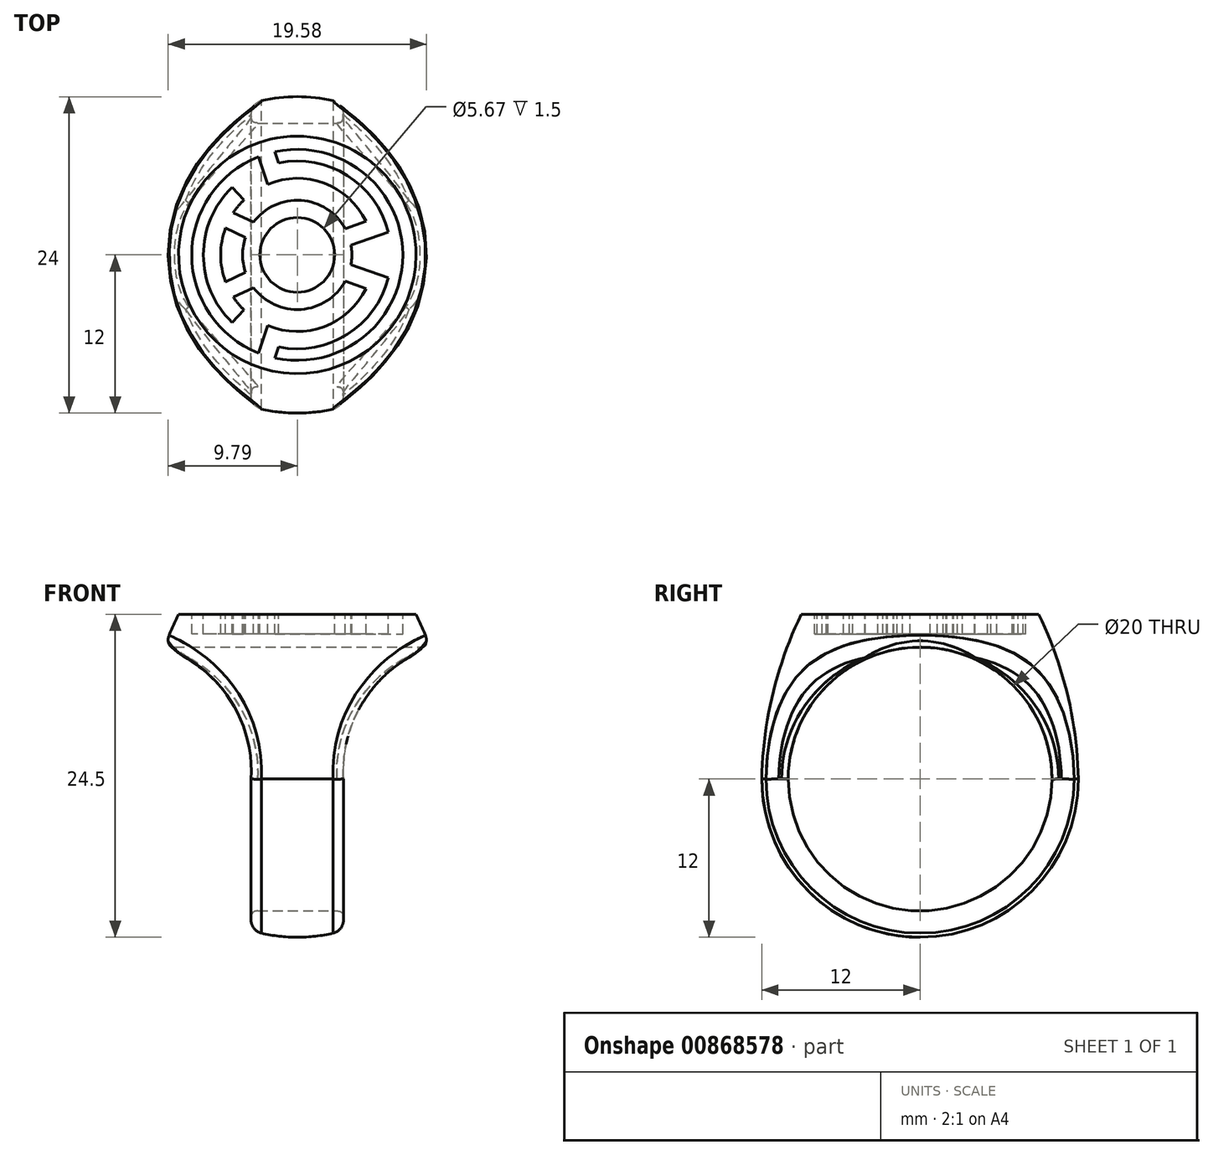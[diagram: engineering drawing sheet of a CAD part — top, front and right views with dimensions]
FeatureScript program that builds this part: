
annotation { "Feature Type Name" : "Feature", "Feature Type Description" : "" }
export const myFeature = defineFeature(function(context is Context, id is Id, definition is map)
    precondition{}
    {
        {
            var Q0;
            Q0=qCreatedBy(makeId("Right.planeOp"),FACE);
            var sketch = newSketch(context, id + "F0", { "sketchPlane" : qUnion([Q0])});
            skLineSegment(sketch, "E0", {"start": v(0, 0) * mm, "end": v(0, -24.5) * mm});
            skLineSegment(sketch, "E1", {"start": v(0, 0) * mm, "end": v(-9, 0) * mm});
            skArc(sketch, "E2", {"start": v(-12, -12.5) * mm, "mid": v(-8.49, -20.99) * mm, "end": v(0, -24.5) * mm});
            skLineSegment(sketch, "E3", {"start": v(0, -12.5) * mm, "end": v(-12, -12.5) * mm, "construction": true});
            skArc(sketch, "E4", {"start": v(-9, 0) * mm, "mid": v(-11.18, -6.09) * mm, "end": v(-12, -12.5) * mm});
            skSolve(sketch);
        }
        {
            var Q0;
            Q0=makeQuery(id+"F0.imprint","IMPRINT",FACE,{"disambiguationData":[TD([[makeQuery(id+"F0.imprint","IMPRINT",EDGE,{"derivedFrom":sQuery(id+"F0.wireOp",EDGE,"E0")}),-1.0]])]});
            var Q1;
            Q1=sQuery(id+"F0.wireOp",EDGE,"E0");
            revolve(context, id + "F1", {"entities" : qUnion([Q0]), "axis" : qUnion([Q1]), "revolveType" : RevolveType.FULL});
        }
        {
            var Q0;
            Q0=qCreatedBy(makeId("Right.planeOp"),FACE);
            var sketch = newSketch(context, id + "F2", { "sketchPlane" : qUnion([Q0])});
            skCircle(sketch, "E5", {"center": v(0, -12.5) * mm, "radius": 10 * mm});
            skSolve(sketch);
        }
        {
            var Q0;
            Q0=qSketchRegion(id+"F2",true);
            extrude(context, id + "F3", {"entities" : qUnion([Q0]), "operationType" : NewBodyOperationType.REMOVE, "endBound" : BoundingType.SYMMETRIC, "oppositeDirection" : true, "depth" : 25 * mm, "offsetDistance" : 25 * mm});
        }
        {
            var Q0;
            Q0=qCreatedBy(makeId("Front.planeOp"),FACE);
            var sketch = newSketch(context, id + "F4", { "sketchPlane" : qUnion([Q0])});
            skLineSegment(sketch, "E6", {"start": v(3.5, -26.5) * mm, "end": v(3.5, -12.5) * mm});
            skArc(sketch, "E7", {"start": v(10.15, -2.5) * mm, "mid": v(5.16, -6.39) * mm, "end": v(3.5, -12.5) * mm});
            skLineSegment(sketch, "E8", {"start": v(10.15, -2.5) * mm, "end": v(11.65, -2.5) * mm});
            skLineSegment(sketch, "E9", {"start": v(11.65, -2.5) * mm, "end": v(11.65, -26.5) * mm});
            skLineSegment(sketch, "E10", {"start": v(11.65, -26.5) * mm, "end": v(3.5, -26.5) * mm});
            skPoint(sketch, "E11.start.orphan", {"position": v(0, -24.5) * mm});
            skLineSegment(sketch, "E12", {"start": v(0, 0) * mm, "end": v(0, -24.5) * mm, "construction": true});
            skLineSegment(sketch, "E13.MirrorCS", {"start": v(-3.5, -26.5) * mm, "end": v(-3.5, -12.5) * mm});
            skArc(sketch, "E14.MirrorCS", {"start": v(-10.15, -2.5) * mm, "mid": v(-5.16, -6.39) * mm, "end": v(-3.5, -12.5) * mm});
            skLineSegment(sketch, "E15.MirrorCS", {"start": v(-11.65, -2.5) * mm, "end": v(-11.65, -26.5) * mm});
            skLineSegment(sketch, "E16.MirrorCS", {"start": v(-11.65, -26.5) * mm, "end": v(-3.5, -26.5) * mm});
            skLineSegment(sketch, "E17.MirrorCS", {"start": v(-10.15, -2.5) * mm, "end": v(-11.65, -2.5) * mm});
            skSolve(sketch);
        }
        {
            var Q0;
            Q0=qSketchRegion(id+"F4",true);
            extrude(context, id + "F5", {"entities" : qUnion([Q0]), "operationType" : NewBodyOperationType.REMOVE, "endBound" : BoundingType.SYMMETRIC, "depth" : 25 * mm, "offsetDistance" : 25 * mm});
        }
        {
            var Q0;
            Q0=makeQuery(id+"F1.opRevolve","SWEPT_FACE",FACE,{"disambiguationData":[OSD([sQuery(id+"F0.wireOp",EDGE,"E1")])]});
            var sketch = newSketch(context, id + "F6", { "sketchPlane" : qUnion([Q0])});
            skLineSegment(sketch, "E18", {"start": v(-8, 0) * mm, "end": v(8, 0) * mm, "construction": true});
            skArc(sketch, "E19", {"start": v(-2.95, 7.44) * mm, "mid": v(-8, 0) * mm, "end": v(-2.95, -7.44) * mm});
            skArc(sketch, "E20", {"start": v(-4.95, 5.12) * mm, "mid": v(-6.55, 2.78) * mm, "end": v(-7.12, 0) * mm});
            skArc(sketch, "E21", {"start": v(5.22, 2.54) * mm, "mid": v(2.05, 5.44) * mm, "end": v(-2.25, 5.36) * mm});
            skArc(sketch, "E22", {"start": v(3.63, 1.99) * mm, "mid": v(0.3, 4.13) * mm, "end": v(-3.32, 2.48) * mm});
            skArc(sketch, "E23", {"start": v(2.83, 0) * mm, "mid": v(0, 2.83) * mm, "end": v(-2.83, 0) * mm});
            skLineSegment(sketch, "E24", {"start": v(6.9, 1.74) * mm, "end": v(4.07, 0.75) * mm});
            skLineSegment(sketch, "E25", {"start": v(5.22, 2.54) * mm, "end": v(3.63, 1.99) * mm});
            skLineSegment(sketch, "E26", {"start": v(-3.32, 2.48) * mm, "end": v(-4.84, 3.2) * mm});
            skLineSegment(sketch, "E27", {"start": v(-3.93, 1.32) * mm, "end": v(-5.44, 2.04) * mm});
            skLineSegment(sketch, "E28", {"start": v(-1.7, 7.82) * mm, "end": v(-1.41, 6.98) * mm});
            skLineSegment(sketch, "E29", {"start": v(-2.25, 5.36) * mm, "end": v(-2.95, 7.44) * mm});
            skArc(sketch, "E30.trimOffspring", {"start": v(-3.93, 1.32) * mm, "mid": v(-4.09, 0.67) * mm, "end": v(-4.14, 0) * mm});
            skArc(sketch, "E31.trimOffspring", {"start": v(-5.44, 2.04) * mm, "mid": v(-5.71, 1.04) * mm, "end": v(-5.8, 0) * mm});
            skArc(sketch, "E32.trimOffspring", {"start": v(6.9, 1.74) * mm, "mid": v(3.8, 6.02) * mm, "end": v(-1.41, 6.98) * mm});
            skArc(sketch, "E33.trimOffspring", {"start": v(4.14, 0) * mm, "mid": v(4.13, 0.38) * mm, "end": v(4.07, 0.75) * mm});
            skLineSegment(sketch, "E34", {"start": v(-4.95, 5.12) * mm, "end": v(-4.04, 4.17) * mm});
            skArc(sketch, "E35.trimOffspring", {"start": v(-4.04, 4.17) * mm, "mid": v(-4.47, 3.71) * mm, "end": v(-4.84, 3.2) * mm});
            skArc(sketch, "E36.MirrorCS", {"start": v(2.83, 0) * mm, "mid": v(0, -2.83) * mm, "end": v(-2.83, 0) * mm});
            skArc(sketch, "E37.MirrorCS", {"start": v(4.14, 0) * mm, "mid": v(4.13, -0.38) * mm, "end": v(4.07, -0.75) * mm});
            skLineSegment(sketch, "E38.MirrorCS", {"start": v(6.9, -1.74) * mm, "end": v(4.07, -0.75) * mm});
            skArc(sketch, "E39.MirrorCS", {"start": v(6.9, -1.74) * mm, "mid": v(3.8, -6.02) * mm, "end": v(-1.41, -6.98) * mm});
            skLineSegment(sketch, "E40.MirrorCS", {"start": v(-1.7, -7.82) * mm, "end": v(-1.41, -6.98) * mm});
            skLineSegment(sketch, "E41.MirrorCS", {"start": v(-2.25, -5.36) * mm, "end": v(-2.95, -7.44) * mm});
            skArc(sketch, "E42.MirrorCS", {"start": v(5.22, -2.54) * mm, "mid": v(2.05, -5.44) * mm, "end": v(-2.25, -5.36) * mm});
            skLineSegment(sketch, "E43.MirrorCS", {"start": v(5.22, -2.54) * mm, "end": v(3.63, -1.99) * mm});
            skArc(sketch, "E44.MirrorCS", {"start": v(3.63, -1.99) * mm, "mid": v(0.3, -4.13) * mm, "end": v(-3.32, -2.48) * mm});
            skLineSegment(sketch, "E45.MirrorCS", {"start": v(-3.32, -2.48) * mm, "end": v(-4.84, -3.2) * mm});
            skArc(sketch, "E46.MirrorCS", {"start": v(-4.04, -4.17) * mm, "mid": v(-4.47, -3.71) * mm, "end": v(-4.84, -3.2) * mm});
            skLineSegment(sketch, "E47.MirrorCS", {"start": v(-4.95, -5.12) * mm, "end": v(-4.04, -4.17) * mm});
            skArc(sketch, "E48.MirrorCS", {"start": v(-4.95, -5.12) * mm, "mid": v(-6.55, -2.78) * mm, "end": v(-7.12, 0) * mm});
            skArc(sketch, "E49.MirrorCS", {"start": v(-3.93, -1.32) * mm, "mid": v(-4.09, -0.67) * mm, "end": v(-4.14, 0) * mm});
            skLineSegment(sketch, "E50.MirrorCS", {"start": v(-3.93, -1.32) * mm, "end": v(-5.44, -2.04) * mm});
            skArc(sketch, "E51.MirrorCS", {"start": v(-5.44, -2.04) * mm, "mid": v(-5.71, -1.04) * mm, "end": v(-5.8, 0) * mm});
            skArc(sketch, "E52.trimOffspring", {"start": v(-1.7, -7.82) * mm, "mid": v(8, 0) * mm, "end": v(-1.7, 7.82) * mm});
            skSolve(sketch);
        }
        {
            var Q0;
            Q0=qSketchRegion(id+"F6",true);
            var Q1;
            Q1=makeQuery(id+"F6.imprint","IMPRINT",FACE,{"disambiguationData":[TD([[makeQuery(id+"F6.imprint","IMPRINT",EDGE,{"derivedFrom":sQuery(id+"F6.wireOp",EDGE,"g20j87Mm-wGr7-AMiz-bI8b-qS7GuHKO57cL")}),1.0]])]});
            extrude(context, id + "F7", {"entities" : qUnion([Q0, Q1]), "operationType" : NewBodyOperationType.REMOVE, "oppositeDirection" : true, "depth" : 1.5 * mm, "offsetDistance" : 25 * mm});
        }
        {
            var Q0;
            Q0=makeQuery(id+"F5.boolean.opBoolean","INTERSECT",EDGE,{"disambiguationData":[OD(1.0)],"derivedFrom":[makeQuery(id+"F1.opRevolve","SWEPT_FACE",FACE,{"disambiguationData":[OSD([sQuery(id+"F0.wireOp",EDGE,"E4")])]}),makeQuery(id+"F5.opExtrude","SWEPT_FACE",FACE,{"disambiguationData":[OSD([sQuery(id+"F4.wireOp",EDGE,"E14.MirrorCS")])]})]});
            var Q1;
            Q1=makeQuery(id+"F5.boolean.opBoolean","INTERSECT",EDGE,{"derivedFrom":[makeQuery(id+"F1.opRevolve","SWEPT_FACE",FACE,{"disambiguationData":[OSD([sQuery(id+"F0.wireOp",EDGE,"E2")])]}),makeQuery(id+"F5.opExtrude","SWEPT_FACE",FACE,{"disambiguationData":[OSD([sQuery(id+"F4.wireOp",EDGE,"E13.MirrorCS")])]})]});
            var Q2;
            Q2=makeQuery(id+"F5.boolean.opBoolean","INTERSECT",EDGE,{"disambiguationData":[OD(1.0)],"derivedFrom":[makeQuery(id+"F1.opRevolve","SWEPT_FACE",FACE,{"disambiguationData":[OSD([sQuery(id+"F0.wireOp",EDGE,"E4")])]}),makeQuery(id+"F5.opExtrude","SWEPT_FACE",FACE,{"disambiguationData":[OSD([sQuery(id+"F4.wireOp",EDGE,"E7")])]})]});
            var Q3;
            Q3=makeQuery(id+"F5.boolean.opBoolean","INTERSECT",EDGE,{"derivedFrom":[makeQuery(id+"F1.opRevolve","SWEPT_FACE",FACE,{"disambiguationData":[OSD([sQuery(id+"F0.wireOp",EDGE,"E2")])]}),makeQuery(id+"F5.opExtrude","SWEPT_FACE",FACE,{"disambiguationData":[OSD([sQuery(id+"F4.wireOp",EDGE,"E6")])]})]});
            fillet(context, id + "F8", {"entities" : qUnion([Q0, Q1, Q2, Q3]), "radius" : 1 * mm, "allowEdgeOverflow" : false});
        }
        {
            var Q0;
            Q0=makeQuery(id+"F5.boolean.opBoolean","INTERSECT",EDGE,{"disambiguationData":[OD(1.0)],"derivedFrom":[makeQuery(id+"F3.boolean.opBoolean","COPY",FACE,{"derivedFrom":makeQuery(id+"F3.opExtrude","SWEPT_FACE",FACE,{"disambiguationData":[OSD([sQuery(id+"F2.wireOp",EDGE,"E5")])]})}),makeQuery(id+"F5.opExtrude","SWEPT_FACE",FACE,{"disambiguationData":[OSD([sQuery(id+"F4.wireOp",EDGE,"E14.MirrorCS")])]})]});
            var Q1;
            Q1=makeQuery(id+"F5.boolean.opBoolean","INTERSECT",EDGE,{"derivedFrom":[makeQuery(id+"F3.boolean.opBoolean","COPY",FACE,{"derivedFrom":makeQuery(id+"F3.opExtrude","SWEPT_FACE",FACE,{"disambiguationData":[OSD([sQuery(id+"F2.wireOp",EDGE,"E5")])]})}),makeQuery(id+"F5.opExtrude","SWEPT_FACE",FACE,{"disambiguationData":[OSD([sQuery(id+"F4.wireOp",EDGE,"E13.MirrorCS")])]})]});
            var Q2;
            Q2=makeQuery(id+"F5.boolean.opBoolean","INTERSECT",EDGE,{"disambiguationData":[OD(0.0)],"derivedFrom":[makeQuery(id+"F3.boolean.opBoolean","COPY",FACE,{"derivedFrom":makeQuery(id+"F3.opExtrude","SWEPT_FACE",FACE,{"disambiguationData":[OSD([sQuery(id+"F2.wireOp",EDGE,"E5")])]})}),makeQuery(id+"F5.opExtrude","SWEPT_FACE",FACE,{"disambiguationData":[OSD([sQuery(id+"F4.wireOp",EDGE,"E14.MirrorCS")])]})]});
            var Q3;
            Q3=makeQuery(id+"F5.boolean.opBoolean","INTERSECT",EDGE,{"disambiguationData":[OD(0.0)],"derivedFrom":[makeQuery(id+"F3.boolean.opBoolean","COPY",FACE,{"derivedFrom":makeQuery(id+"F3.opExtrude","SWEPT_FACE",FACE,{"disambiguationData":[OSD([sQuery(id+"F2.wireOp",EDGE,"E5")])]})}),makeQuery(id+"F5.opExtrude","SWEPT_FACE",FACE,{"disambiguationData":[OSD([sQuery(id+"F4.wireOp",EDGE,"E7")])]})]});
            var Q4;
            Q4=makeQuery(id+"F3.boolean.opBoolean","COPY",FACE,{"derivedFrom":makeQuery(id+"F3.opExtrude","SWEPT_FACE",FACE,{"disambiguationData":[OSD([sQuery(id+"F2.wireOp",EDGE,"E5")])]})});
            fillet(context, id + "F9", {"entities" : qUnion([Q0, Q1, Q2, Q3, Q4]), "radius" : .5 * mm, "rho" : 0.5, "crossSection" : FilletCrossSection.CONIC, "allowEdgeOverflow" : false});
        }
    });
